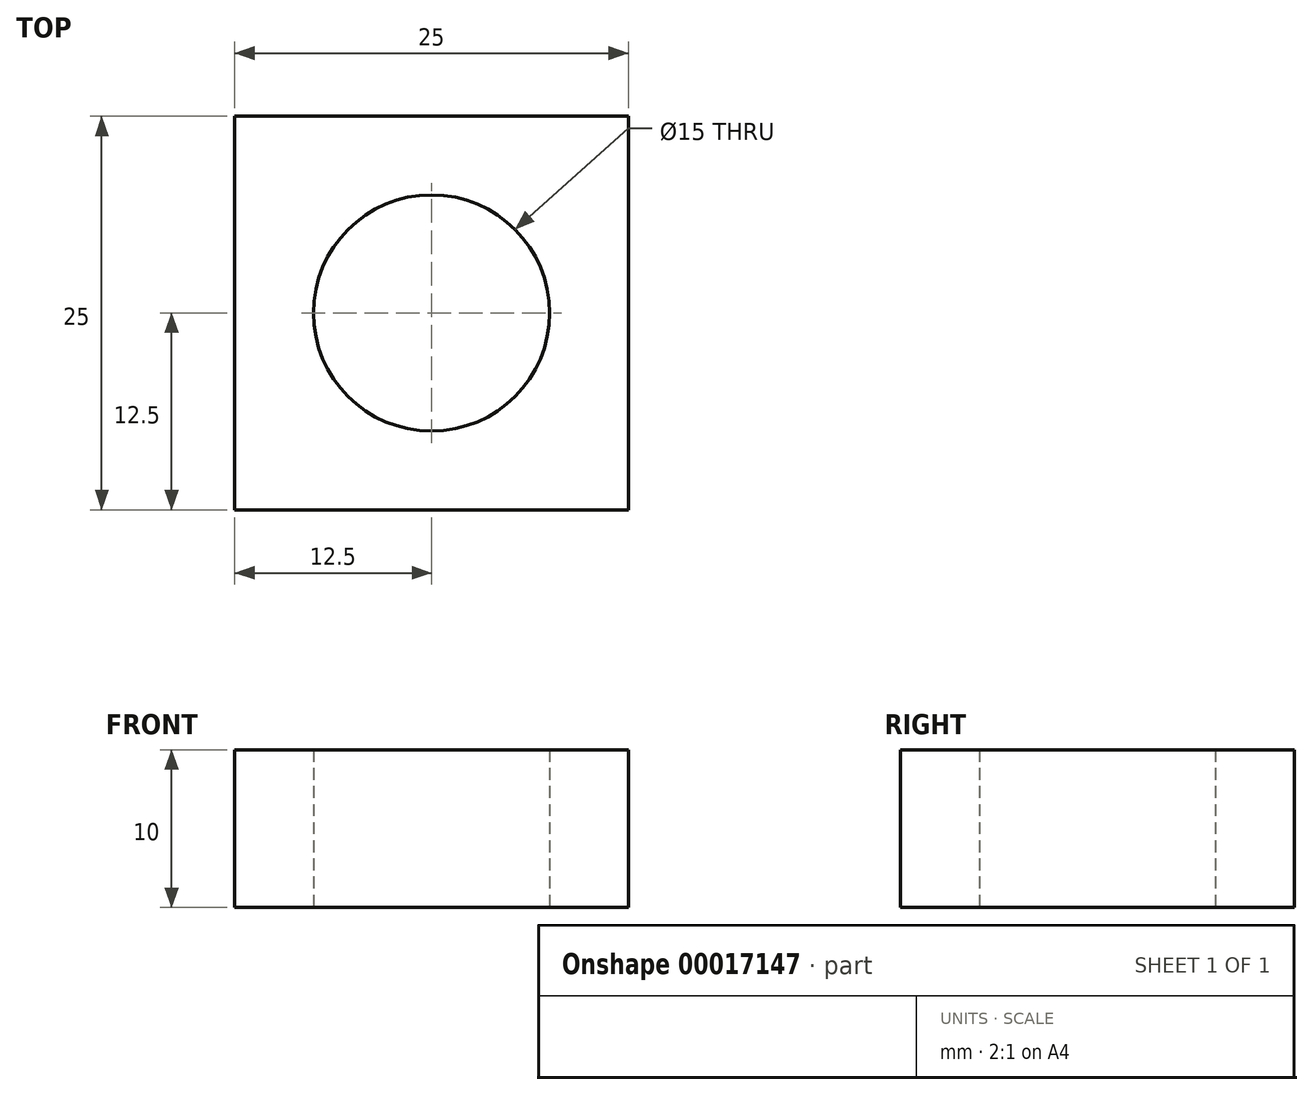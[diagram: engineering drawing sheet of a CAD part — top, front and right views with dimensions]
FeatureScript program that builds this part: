
annotation { "Feature Type Name" : "Feature", "Feature Type Description" : "" }
export const myFeature = defineFeature(function(context is Context, id is Id, definition is map)
    precondition{}
    {
        {
            var Q0;
            Q0=qCreatedBy(makeId("Top.planeOp"),FACE);
            var sketch = newSketch(context, id + "F0", { "sketchPlane" : qUnion([Q0])});
            skLineSegment(sketch, "E0.rect.bottom", {"start": v(-12.5, -12.5) * mm, "end": v(12.5, -12.5) * mm});
            skLineSegment(sketch, "E0.rect.top", {"start": v(-12.5, 12.5) * mm, "end": v(12.5, 12.5) * mm});
            skLineSegment(sketch, "E0.rect.left", {"start": v(-12.5, -12.5) * mm, "end": v(-12.5, 12.5) * mm});
            skLineSegment(sketch, "E0.rect.right", {"start": v(12.5, -12.5) * mm, "end": v(12.5, 12.5) * mm});
            skPoint(sketch, "E0.rect.middle", {"position": v(0, 0) * mm});
            skCircle(sketch, "E1", {"center": v(0, 0) * mm, "radius": 7.5 * mm});
            skSolve(sketch);
        }
        {
            var Q0;
            Q0=makeQuery(id+"F0.imprint","IMPRINT",FACE,{"disambiguationData":[TD([[makeQuery(id+"F0.imprint","IMPRINT",EDGE,{"derivedFrom":sQuery(id+"F0.wireOp",EDGE,"E0.rect.bottom")}),1.0]])]});
            extrude(context, id + "F1", {"entities" : qUnion([Q0]), "depth" : 10 * mm});
        }
    });
